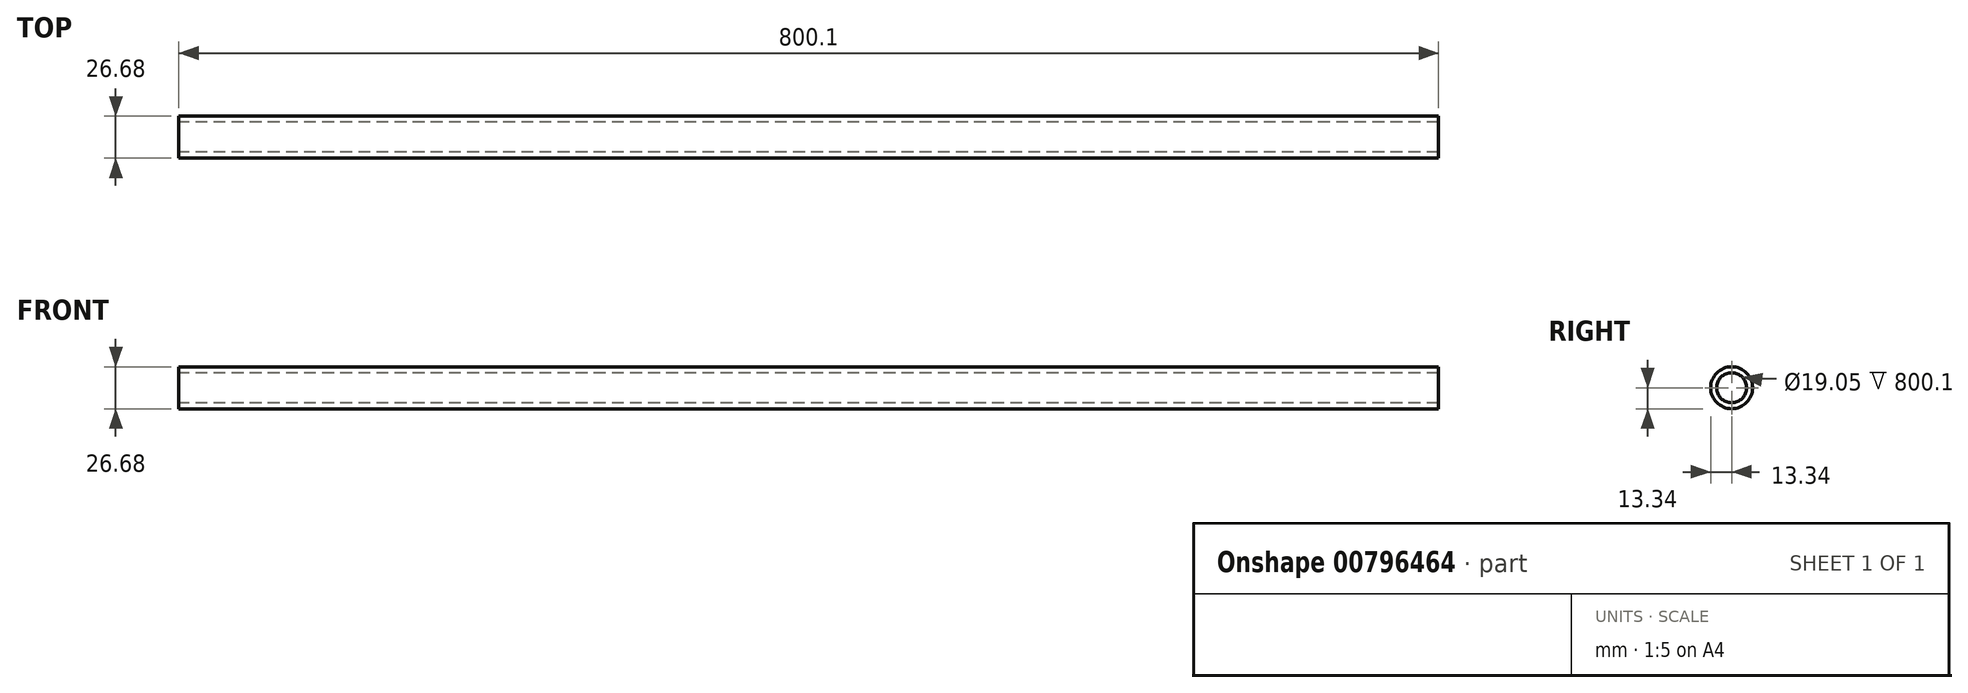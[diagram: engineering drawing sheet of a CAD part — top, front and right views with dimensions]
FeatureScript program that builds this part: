
annotation { "Feature Type Name" : "Feature", "Feature Type Description" : "" }
export const myFeature = defineFeature(function(context is Context, id is Id, definition is map)
    precondition{}
    {
        {
            var Q0;
            Q0=qCreatedBy(makeId("Right.planeOp"),FACE);
            var sketch = newSketch(context, id + "F0", { "sketchPlane" : qUnion([Q0])});
            skCircle(sketch, "E0", {"center": v(0, 0) * mm, "radius": 9.53 * mm});
            skCircle(sketch, "E1.0", {"center": v(0, 0) * mm, "radius": 13.33 * mm});
            skSolve(sketch);
        }
        {
            var Q0;
            Q0=qSketchRegion(id+"F0",true);
            extrude(context, id + "F1", {"entities" : qUnion([Q0]), "depth" : 800.1 * mm, "offsetDistance" : 25.4 * mm});
        }
    });
